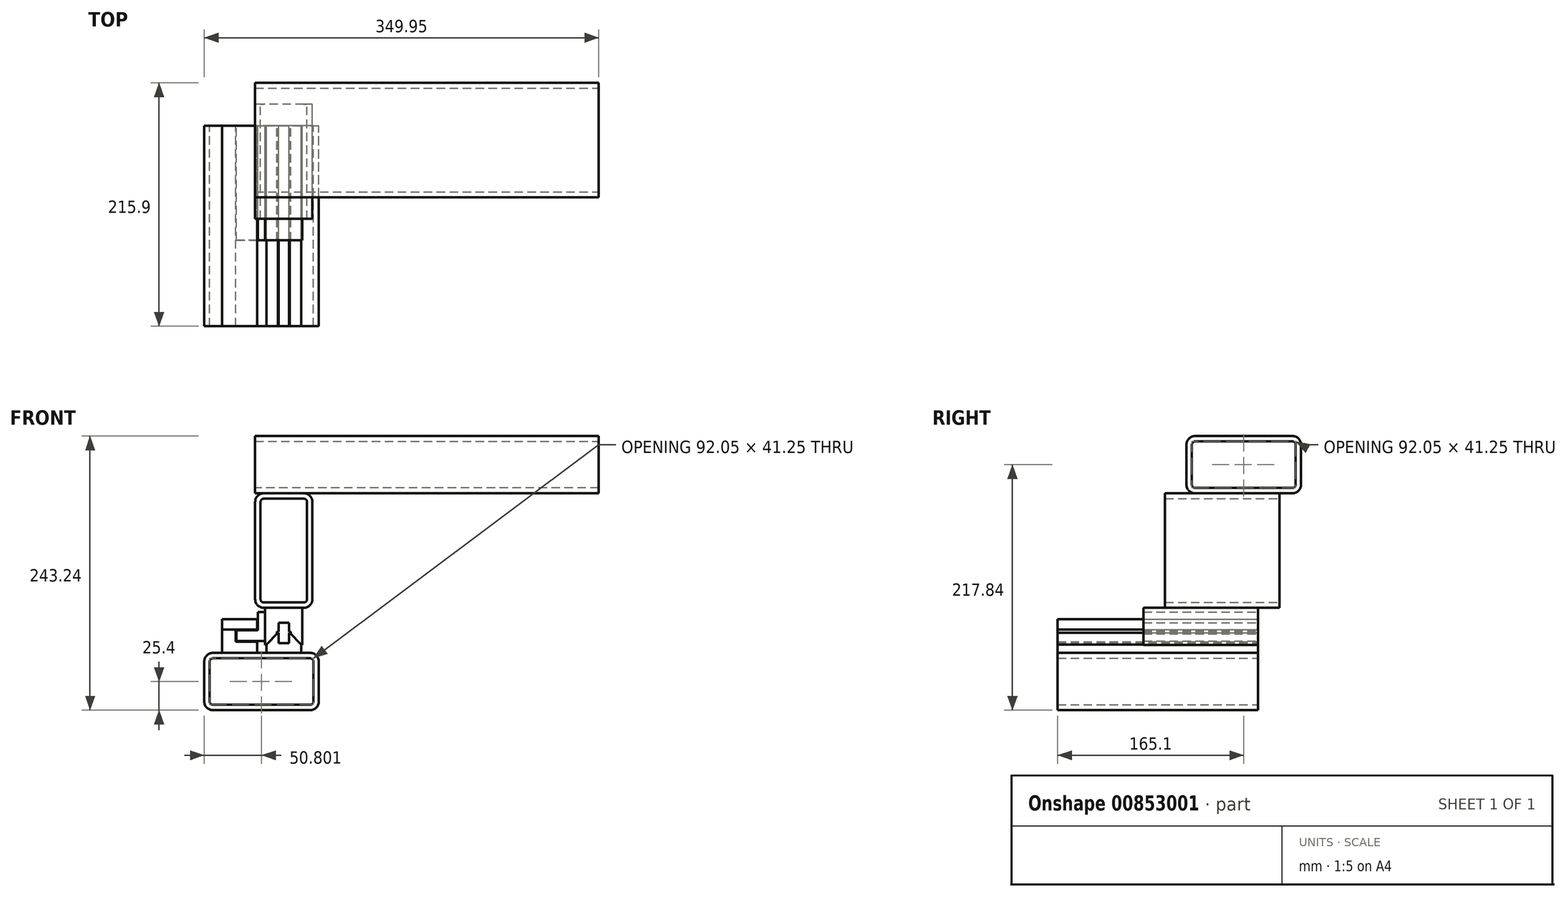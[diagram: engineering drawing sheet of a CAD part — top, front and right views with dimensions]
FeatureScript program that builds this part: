
annotation { "Feature Type Name" : "Feature", "Feature Type Description" : "" }
export const myFeature = defineFeature(function(context is Context, id is Id, definition is map)
    precondition{}
    {
        {
            var Q0;
            Q0=qCreatedBy(makeId("Front.planeOp"),FACE);
            var sketch = newSketch(context, id + "F0", { "sketchPlane" : qUnion([Q0])});
            skLineSegment(sketch, "E0", {"start": v(0, 0) * mm, "end": v(15.36, 0) * mm});
            skLineSegment(sketch, "E1", {"start": v(15.36, 0) * mm, "end": v(15.36, 7.56) * mm});
            skLineSegment(sketch, "E2", {"start": v(15.36, 7.56) * mm, "end": v(5.14, 17.78) * mm});
            skLineSegment(sketch, "E3", {"start": v(5.14, 17.78) * mm, "end": v(4.5, 17.78) * mm});
            skLineSegment(sketch, "E4", {"start": v(4.5, 17.78) * mm, "end": v(4.5, 8.78) * mm});
            skLineSegment(sketch, "E5", {"start": v(4.5, 8.78) * mm, "end": v(0, 8.78) * mm});
            skLineSegment(sketch, "E6", {"start": v(15.36, 7.56) * mm, "end": v(15.9, 7.02) * mm});
            skLineSegment(sketch, "E7", {"start": v(15.9, 7.02) * mm, "end": v(16.51, 7.02) * mm});
            skLineSegment(sketch, "E8", {"start": v(16.51, 7.02) * mm, "end": v(16.51, 40.04) * mm});
            skLineSegment(sketch, "E9", {"start": v(16.51, 40.04) * mm, "end": v(0, 40.04) * mm});
            skLineSegment(sketch, "E10", {"start": v(6.12, 16.8) * mm, "end": v(6.12, 18.78) * mm});
            skLineSegment(sketch, "E11", {"start": v(6.12, 18.78) * mm, "end": v(4.5, 18.78) * mm});
            skLineSegment(sketch, "E12", {"start": v(4.5, 18.78) * mm, "end": v(4.5, 26.78) * mm});
            skLineSegment(sketch, "E13", {"start": v(4.5, 26.78) * mm, "end": v(0, 26.78) * mm});
            skLineSegment(sketch, "E14.MirrorCS", {"start": v(-4.5, 8.78) * mm, "end": v(0, 8.78) * mm});
            skLineSegment(sketch, "E15.MirrorCS", {"start": v(0, 0) * mm, "end": v(-15.36, 0) * mm});
            skLineSegment(sketch, "E16.MirrorCS", {"start": v(-15.36, 0) * mm, "end": v(-15.36, 7.56) * mm});
            skLineSegment(sketch, "E17.MirrorCS", {"start": v(-4.5, 17.78) * mm, "end": v(-4.5, 8.78) * mm});
            skLineSegment(sketch, "E18.MirrorCS", {"start": v(-5.14, 17.78) * mm, "end": v(-4.5, 17.78) * mm});
            skLineSegment(sketch, "E19.MirrorCS", {"start": v(-15.36, 7.56) * mm, "end": v(-5.14, 17.78) * mm});
            skLineSegment(sketch, "E20.MirrorCS", {"start": v(-6.12, 16.8) * mm, "end": v(-6.12, 18.78) * mm});
            skLineSegment(sketch, "E21.MirrorCS", {"start": v(-6.12, 18.78) * mm, "end": v(-4.5, 18.78) * mm});
            skLineSegment(sketch, "E22.MirrorCS", {"start": v(-4.5, 18.78) * mm, "end": v(-4.5, 26.78) * mm});
            skLineSegment(sketch, "E23.MirrorCS", {"start": v(-15.9, 7.02) * mm, "end": v(-16.51, 7.02) * mm});
            skLineSegment(sketch, "E24.MirrorCS", {"start": v(-16.51, 7.02) * mm, "end": v(-16.51, 40.04) * mm});
            skLineSegment(sketch, "E25.MirrorCS", {"start": v(-4.5, 26.78) * mm, "end": v(0, 26.78) * mm});
            skLineSegment(sketch, "E26.MirrorCS", {"start": v(-16.51, 40.04) * mm, "end": v(0, 40.04) * mm});
            skLineSegment(sketch, "E27", {"start": v(5.14, 17.78) * mm, "end": v(0, 22.92) * mm, "construction": true});
            skLineSegment(sketch, "E28", {"start": v(-15.36, 7.56) * mm, "end": v(-15.9, 7.02) * mm});
            skSolve(sketch);
        }
        {
            var Q0;
            Q0=makeQuery(id+"F0.imprint","IMPRINT",FACE,{"disambiguationData":[TD([[makeQuery(id+"F0.imprint","IMPRINT",EDGE,{"derivedFrom":sQuery(id+"F0.wireOp",EDGE,"E0")}),1.0]])]});
            extrude(context, id + "F1", {"entities" : qUnion([Q0]), "depth" : 177.8 * mm, "offsetDistance" : 25.4 * mm});
        }
        {
            var Q0;
            {var subQ2=sQuery(id+"F0.wireOp",EDGE,"E7");Q0=makeQuery(id+"F0.imprint","IMPRINT",FACE,{"disambiguationData":[TD([[makeQuery(id+"F0.imprint","IMPRINT",EDGE,{"derivedFrom":subQ2}),1.0]])]});}
            extrude(context, id + "F2", {"entities" : qUnion([Q0]), "depth" : 101.6 * mm, "offsetDistance" : 25.4 * mm});
        }
        {
            var Q0;
            Q0=qCreatedBy(makeId("Front.planeOp"),FACE);
            var sketch = newSketch(context, id + "F3", { "sketchPlane" : qUnion([Q0])});
            skLineSegment(sketch, "E29.0", {"start": v(-15.36, 0) * mm, "end": v(-15.36, 7.56) * mm});
            skLineSegment(sketch, "E30", {"start": v(-15.36, 0) * mm, "end": v(-54.86, 0) * mm});
            skLineSegment(sketch, "E31", {"start": v(-54.86, 0) * mm, "end": v(-54.86, 29.93) * mm});
            skLineSegment(sketch, "E32", {"start": v(-54.86, 29.93) * mm, "end": v(-23.64, 29.93) * mm});
            skLineSegment(sketch, "E33", {"start": v(-23.64, 29.93) * mm, "end": v(-23.64, 20.74) * mm});
            skLineSegment(sketch, "E34", {"start": v(-23.64, 20.74) * mm, "end": v(-42.7, 20.74) * mm});
            skLineSegment(sketch, "E35", {"start": v(-42.7, 20.74) * mm, "end": v(-54.86, 20.74) * mm});
            skLineSegment(sketch, "E36.0", {"start": v(-16.51, 7.02) * mm, "end": v(-16.51, 40.04) * mm});
            skLineSegment(sketch, "E37", {"start": v(-41.93, 19.98) * mm, "end": v(-41.93, 10.63) * mm});
            skLineSegment(sketch, "E38", {"start": v(-41.93, 10.63) * mm, "end": v(-16.51, 10.63) * mm});
            skLineSegment(sketch, "E39", {"start": v(-22.86, 19.98) * mm, "end": v(-22.86, 36.45) * mm});
            skLineSegment(sketch, "E40", {"start": v(-22.86, 36.45) * mm, "end": v(-16.51, 36.29) * mm});
            skLineSegment(sketch, "E41", {"start": v(-22.86, 19.98) * mm, "end": v(-41.93, 19.98) * mm});
            skLineSegment(sketch, "E42", {"start": v(-23.64, 7.56) * mm, "end": v(-23.64, 9.87) * mm});
            skLineSegment(sketch, "E43", {"start": v(-23.64, 9.87) * mm, "end": v(-42.7, 9.87) * mm});
            skLineSegment(sketch, "E44", {"start": v(-42.7, 9.87) * mm, "end": v(-42.7, 20.74) * mm});
            skLineSegment(sketch, "E45", {"start": v(-42.7, 15.75) * mm, "end": v(-41.93, 15.75) * mm, "construction": true});
            skLineSegment(sketch, "E46", {"start": v(-33.1, 20.74) * mm, "end": v(-33.1, 19.98) * mm, "construction": true});
            skLineSegment(sketch, "E47", {"start": v(-28.61, 9.87) * mm, "end": v(-28.61, 10.63) * mm, "construction": true});
            skLineSegment(sketch, "E48", {"start": v(-23.64, 7.56) * mm, "end": v(-23.64, 4.69) * mm});
            skLineSegment(sketch, "E49", {"start": v(-23.64, 4.69) * mm, "end": v(-23.64, 0) * mm});
            skLineSegment(sketch, "E50", {"start": v(-54.86, 0) * mm, "end": v(-54.86, -7.97) * mm});
            skLineSegment(sketch, "E51", {"start": v(-54.86, -7.97) * mm, "end": v(20.19, -7.97) * mm});
            skLineSegment(sketch, "E52", {"start": v(20.19, -7.97) * mm, "end": v(20.19, 0) * mm});
            skLineSegment(sketch, "E53", {"start": v(20.19, 0) * mm, "end": v(-15.36, 0) * mm});
            skSolve(sketch);
        }
        {
            var Q0;
            Q0=makeQuery(id+"F3.imprint","IMPRINT",FACE,{"disambiguationData":[TD([[makeQuery(id+"F3.imprint","IMPRINT",EDGE,{"derivedFrom":sQuery(id+"F3.wireOp",EDGE,"E37")}),1.0]])]});
            var Q1;
            Q1=makeQuery(id+"F2.opExtrude","CAP_FACE",FACE,{"disambiguationData":[OSD([sQuery(id+"F0.wireOp",EDGE,"E2"),sQuery(id+"F0.wireOp",EDGE,"E7"),sQuery(id+"F0.wireOp",EDGE,"E8"),sQuery(id+"F0.wireOp",EDGE,"E9"),sQuery(id+"F0.wireOp",EDGE,"E10"),sQuery(id+"F0.wireOp",EDGE,"E11"),sQuery(id+"F0.wireOp",EDGE,"E12"),sQuery(id+"F0.wireOp",EDGE,"E13"),sQuery(id+"F0.wireOp",EDGE,"E19.MirrorCS"),sQuery(id+"F0.wireOp",EDGE,"E20.MirrorCS"),sQuery(id+"F0.wireOp",EDGE,"E21.MirrorCS"),sQuery(id+"F0.wireOp",EDGE,"E22.MirrorCS"),sQuery(id+"F0.wireOp",EDGE,"E23.MirrorCS"),sQuery(id+"F0.wireOp",EDGE,"E24.MirrorCS"),sQuery(id+"F0.wireOp",EDGE,"E25.MirrorCS"),sQuery(id+"F0.wireOp",EDGE,"E26.MirrorCS")])],"isStart":false});
            extrude(context, id + "F4", {"entities" : qUnion([Q0]), "endBound" : BoundingType.UP_TO_SURFACE, "depth" : 25.4 * mm, "endBoundEntityFace" : qUnion([Q1]), "offsetDistance" : 25.4 * mm});
        }
        {
            var Q0;
            {var subQ0=sQuery(id+"F3.wireOp",EDGE,"E32");Q0=makeQuery(id+"F3.imprint","IMPRINT",FACE,{"disambiguationData":[TD([[makeQuery(id+"F3.imprint","IMPRINT",EDGE,{"derivedFrom":subQ0}),-1.0]])]});}
            var Q1;
            Q1=makeQuery(id+"F1.opExtrude","CAP_FACE",FACE,{"disambiguationData":[OSD([sQuery(id+"F0.wireOp",EDGE,"E0"),sQuery(id+"F0.wireOp",EDGE,"E1"),sQuery(id+"F0.wireOp",EDGE,"E2"),sQuery(id+"F0.wireOp",EDGE,"E3"),sQuery(id+"F0.wireOp",EDGE,"E4"),sQuery(id+"F0.wireOp",EDGE,"E5"),sQuery(id+"F0.wireOp",EDGE,"E6"),sQuery(id+"F0.wireOp",EDGE,"E14.MirrorCS"),sQuery(id+"F0.wireOp",EDGE,"E15.MirrorCS"),sQuery(id+"F0.wireOp",EDGE,"E16.MirrorCS"),sQuery(id+"F0.wireOp",EDGE,"E17.MirrorCS"),sQuery(id+"F0.wireOp",EDGE,"E18.MirrorCS"),sQuery(id+"F0.wireOp",EDGE,"E19.MirrorCS")])],"isStart":false});
            extrude(context, id + "F5", {"entities" : qUnion([Q0]), "endBound" : BoundingType.UP_TO_SURFACE, "depth" : 25.4 * mm, "endBoundEntityFace" : qUnion([Q1]), "offsetDistance" : 25.4 * mm});
        }
        {
            var Q0;
            {var subQ0=sQuery(id+"F3.wireOp",EDGE,"E35");Q0=makeQuery(id+"F3.imprint","IMPRINT",FACE,{"disambiguationData":[TD([[makeQuery(id+"F3.imprint","IMPRINT",EDGE,{"derivedFrom":subQ0}),1.0]])]});}
            var Q1;
            Q1=makeQuery(id+"F5.opExtrude","CAP_FACE",FACE,{"disambiguationData":[OSD([sQuery(id+"F3.wireOp",EDGE,"E29.0"),sQuery(id+"F3.wireOp",EDGE,"E30"),sQuery(id+"F3.wireOp",EDGE,"E31"),sQuery(id+"F3.wireOp",EDGE,"E35"),sQuery(id+"F3.wireOp",EDGE,"DQE3j6KB-5Aju-39En-5gZ4-T2iJxYTfEG1l"),sQuery(id+"F3.wireOp",EDGE,"E42"),sQuery(id+"F3.wireOp",EDGE,"E43"),sQuery(id+"F3.wireOp",EDGE,"E44")])],"isStart":false});
            extrude(context, id + "F6", {"entities" : qUnion([Q0]), "endBound" : BoundingType.UP_TO_SURFACE, "depth" : 25.4 * mm, "endBoundEntityFace" : qUnion([Q1]), "offsetDistance" : 25.4 * mm});
        }
        {
            var Q0;
            Q0=qCreatedBy(makeId("Front.planeOp"),FACE);
            var sketch = newSketch(context, id + "F7", { "sketchPlane" : qUnion([Q0])});
            skPoint(sketch, "E54.0", {"position": v(15.36, 0) * mm});
            skPoint(sketch, "E55.0", {"position": v(-54.86, 0) * mm});
            skLineSegment(sketch, "E56", {"start": v(-54.86, 0) * mm, "end": v(15.36, 0) * mm, "construction": true});
            skLineSegment(sketch, "E57", {"start": v(-19.75, 0) * mm, "end": v(-19.75, -25.4) * mm, "construction": true});
            skLineSegment(sketch, "E58.bottom", {"start": v(31.05, 0) * mm, "end": v(-70.55, 0) * mm});
            skLineSegment(sketch, "E58.top", {"start": v(31.05, -50.8) * mm, "end": v(-70.55, -50.8) * mm});
            skLineSegment(sketch, "E58.left", {"start": v(31.05, 0) * mm, "end": v(31.05, -50.8) * mm});
            skLineSegment(sketch, "E58.right", {"start": v(-70.55, 0) * mm, "end": v(-70.55, -50.8) * mm});
            skPoint(sketch, "E58.middle", {"position": v(-19.75, -25.4) * mm});
            skSolve(sketch);
        }
        {
            var Q0;
            Q0 = qSketchRegion(id + "F7", true);
            var Q1;
            Q1=makeQuery(id+"F6.opExtrude","CAP_FACE",FACE,{"disambiguationData":[OSD([sQuery(id+"F3.wireOp",EDGE,"E30"),sQuery(id+"F3.wireOp",EDGE,"E31"),sQuery(id+"F3.wireOp",EDGE,"E35"),sQuery(id+"F3.wireOp",EDGE,"E42"),sQuery(id+"F3.wireOp",EDGE,"E43"),sQuery(id+"F3.wireOp",EDGE,"E44"),sQuery(id+"F3.wireOp",EDGE,"E48"),sQuery(id+"F3.wireOp",EDGE,"E49")])],"isStart":false});
            extrude(context, id + "F8", {"entities" : qUnion([Q0]), "endBound" : BoundingType.UP_TO_SURFACE, "depth" : 25.4 * mm, "endBoundEntityFace" : qUnion([Q1]), "offsetDistance" : 25.4 * mm});
        }
        {
            var Q0;
            Q0=makeQuery(id+"F8.opExtrude","SWEPT_EDGE",EDGE,{"disambiguationData":[OSD([sQuery(id+"F7.wireOp",EDGE,"E58.bottom"),sQuery(id+"F7.wireOp",EDGE,"E58.right")])]});
            var Q1;
            Q1=makeQuery(id+"F8.opExtrude","SWEPT_EDGE",EDGE,{"disambiguationData":[OSD([sQuery(id+"F7.wireOp",EDGE,"E58.bottom"),sQuery(id+"F7.wireOp",EDGE,"E58.left")])]});
            var Q2;
            Q2=makeQuery(id+"F8.opExtrude","SWEPT_EDGE",EDGE,{"disambiguationData":[OSD([sQuery(id+"F7.wireOp",EDGE,"E58.top"),sQuery(id+"F7.wireOp",EDGE,"E58.right")])]});
            var Q3;
            Q3=makeQuery(id+"F8.opExtrude","SWEPT_EDGE",EDGE,{"disambiguationData":[OSD([sQuery(id+"F7.wireOp",EDGE,"E58.top"),sQuery(id+"F7.wireOp",EDGE,"E58.left")])]});
            fillet(context, id + "F9", {"entities" : qUnion([Q0, Q1, Q2, Q3]), "radius" : 7.62 * mm, "tangentPropagation" : true, "allowEdgeOverflow" : false});
        }
        {
            var Q0;
            Q0=makeQuery(id+"F8.opExtrude","CAP_FACE",FACE,{"disambiguationData":[OSD([sQuery(id+"F7.wireOp",EDGE,"E58.bottom"),sQuery(id+"F7.wireOp",EDGE,"E58.top"),sQuery(id+"F7.wireOp",EDGE,"E58.left"),sQuery(id+"F7.wireOp",EDGE,"E58.right")])],"isStart":false});
            shell(context, id + "F10", {"entities" : qUnion([Q0]), "thickness" : 4.78 * mm});
        }
        {
            var Q0;
            Q0=makeQuery(id+"F10.opShell","OFFSET_FACE",FACE,{"disambiguationData":[OSD([sQuery(id+"F7.wireOp",EDGE,"E58.bottom"),sQuery(id+"F7.wireOp",EDGE,"E58.top"),sQuery(id+"F7.wireOp",EDGE,"E58.left"),sQuery(id+"F7.wireOp",EDGE,"E58.right")])]});
            extrude(context, id + "F11", {"entities" : qUnion([Q0]), "operationType" : NewBodyOperationType.REMOVE, "oppositeDirection" : true, "depth" : 25.4 * mm, "offsetDistance" : 25.4 * mm});
        }
        {
            var Q0;
            Q0=qCreatedBy(makeId("Front.planeOp"),FACE);
            var sketch = newSketch(context, id + "F12", { "sketchPlane" : qUnion([Q0])});
            skPoint(sketch, "E59.0", {"position": v(0, 40.04) * mm});
            skLineSegment(sketch, "E60.bottom", {"start": v(25.4, 40.04) * mm, "end": v(-25.4, 40.04) * mm});
            skLineSegment(sketch, "E60.top", {"start": v(25.4, 141.64) * mm, "end": v(-25.4, 141.64) * mm});
            skLineSegment(sketch, "E60.left", {"start": v(25.4, 40.04) * mm, "end": v(25.4, 141.64) * mm});
            skLineSegment(sketch, "E60.right", {"start": v(-25.4, 40.04) * mm, "end": v(-25.4, 141.64) * mm});
            skPoint(sketch, "E60.middle", {"position": v(0, 90.84) * mm});
            skSolve(sketch);
        }
        {
            var Q0;
            Q0 = qSketchRegion(id + "F12", true);
            extrude(context, id + "F13", {"entities" : qUnion([Q0]), "depth" : 82.55 * mm, "offsetDistance" : 25.4 * mm, "hasSecondDirection" : true, "secondDirectionOppositeDirection" : true, "secondDirectionDepth" : 19.05 * mm});
        }
        {
            var Q0;
            Q0=makeQuery(id+"F13.opExtrude","SWEPT_EDGE",EDGE,{"disambiguationData":[OSD([sQuery(id+"F12.wireOp",EDGE,"E60.top"),sQuery(id+"F12.wireOp",EDGE,"E60.left")])]});
            var Q1;
            Q1=makeQuery(id+"F13.opExtrude","SWEPT_EDGE",EDGE,{"disambiguationData":[OSD([sQuery(id+"F12.wireOp",EDGE,"E60.bottom"),sQuery(id+"F12.wireOp",EDGE,"E60.left")])]});
            var Q2;
            Q2=makeQuery(id+"F13.opExtrude","SWEPT_EDGE",EDGE,{"disambiguationData":[OSD([sQuery(id+"F12.wireOp",EDGE,"E60.bottom"),sQuery(id+"F12.wireOp",EDGE,"E60.right")])]});
            var Q3;
            Q3=makeQuery(id+"F13.opExtrude","SWEPT_EDGE",EDGE,{"disambiguationData":[OSD([sQuery(id+"F12.wireOp",EDGE,"E60.top"),sQuery(id+"F12.wireOp",EDGE,"E60.right")])]});
            fillet(context, id + "F14", {"entities" : qUnion([Q0, Q1, Q2, Q3]), "radius" : 7.62 * mm, "tangentPropagation" : true, "allowEdgeOverflow" : false});
        }
        {
            var Q0;
            Q0=makeQuery(id+"F13.opExtrude","CAP_FACE",FACE,{"disambiguationData":[OSD([sQuery(id+"F12.wireOp",EDGE,"E60.bottom"),sQuery(id+"F12.wireOp",EDGE,"E60.top"),sQuery(id+"F12.wireOp",EDGE,"E60.left"),sQuery(id+"F12.wireOp",EDGE,"E60.right")])],"isStart":false});
            shell(context, id + "F15", {"entities" : qUnion([Q0]), "thickness" : 4.78 * mm});
        }
        {
            var Q0;
            Q0=makeQuery(id+"F15.opShell","OFFSET_FACE",FACE,{"disambiguationData":[OSD([sQuery(id+"F12.wireOp",EDGE,"E60.bottom"),sQuery(id+"F12.wireOp",EDGE,"E60.top"),sQuery(id+"F12.wireOp",EDGE,"E60.left"),sQuery(id+"F12.wireOp",EDGE,"E60.right")])]});
            extrude(context, id + "F16", {"entities" : qUnion([Q0]), "operationType" : NewBodyOperationType.REMOVE, "oppositeDirection" : true, "depth" : 25.4 * mm, "offsetDistance" : 25.4 * mm});
        }
        {
            var Q0;
            Q0=makeQuery(id+"F13.opExtrude","SWEPT_FACE",FACE,{"disambiguationData":[OSD([sQuery(id+"F12.wireOp",EDGE,"E60.right")])]});
            var sketch = newSketch(context, id + "F17", { "sketchPlane" : qUnion([Q0])});
            skLineSegment(sketch, "E61.0", {"start": v(-19.05, 141.64) * mm, "end": v(82.55, 141.64) * mm});
            skLineSegment(sketch, "E62.bottom", {"start": v(63.5, 141.64) * mm, "end": v(-38.1, 141.64) * mm});
            skLineSegment(sketch, "E62.top", {"start": v(63.5, 192.44) * mm, "end": v(-38.1, 192.44) * mm});
            skLineSegment(sketch, "E62.left", {"start": v(63.5, 141.64) * mm, "end": v(63.5, 192.44) * mm});
            skLineSegment(sketch, "E62.right", {"start": v(-38.1, 141.64) * mm, "end": v(-38.1, 192.44) * mm});
            skPoint(sketch, "E62.middle", {"position": v(12.7, 167.04) * mm});
            skPoint(sketch, "E62.middle.positionSnap0", {"position": v(31.75, 141.64) * mm});
            skPoint(sketch, "E62.centerSnap0", {"position": v(31.75, 141.64) * mm});
            skPoint(sketch, "E63", {"position": v(12.7, 141.64) * mm});
            skSolve(sketch);
        }
        {
            var Q0;
            Q0 = qSketchRegion(id + "F17", true);
            extrude(context, id + "F18", {"entities" : qUnion([Q0]), "oppositeDirection" : true, "depth" : 304.8 * mm, "offsetDistance" : 25.4 * mm});
        }
        {
            var Q0;
            Q0=makeQuery(id+"F18.opExtrude","SWEPT_EDGE",EDGE,{"disambiguationData":[OSD([sQuery(id+"F17.wireOp",EDGE,"E62.bottom"),sQuery(id+"F17.wireOp",EDGE,"E62.right")])]});
            var Q1;
            Q1=makeQuery(id+"F18.opExtrude","SWEPT_EDGE",EDGE,{"disambiguationData":[OSD([sQuery(id+"F17.wireOp",EDGE,"E62.bottom"),sQuery(id+"F17.wireOp",EDGE,"E62.left")])]});
            var Q2;
            Q2=makeQuery(id+"F18.opExtrude","SWEPT_EDGE",EDGE,{"disambiguationData":[OSD([sQuery(id+"F17.wireOp",EDGE,"E62.top"),sQuery(id+"F17.wireOp",EDGE,"E62.left")])]});
            var Q3;
            Q3=makeQuery(id+"F18.opExtrude","SWEPT_EDGE",EDGE,{"disambiguationData":[OSD([sQuery(id+"F17.wireOp",EDGE,"E62.top"),sQuery(id+"F17.wireOp",EDGE,"E62.right")])]});
            fillet(context, id + "F19", {"entities" : qUnion([Q0, Q1, Q2, Q3]), "radius" : 7.62 * mm, "tangentPropagation" : true, "allowEdgeOverflow" : false});
        }
        {
            var Q0;
            Q0=makeQuery(id+"F18.opExtrude","CAP_FACE",FACE,{"disambiguationData":[OSD([sQuery(id+"F17.wireOp",EDGE,"E62.bottom"),sQuery(id+"F17.wireOp",EDGE,"E62.top"),sQuery(id+"F17.wireOp",EDGE,"E62.left"),sQuery(id+"F17.wireOp",EDGE,"E62.right")])],"isStart":true});
            shell(context, id + "F20", {"entities" : qUnion([Q0]), "thickness" : 4.78 * mm});
        }
        {
            var Q0;
            Q0=makeQuery(id+"F20.opShell","OFFSET_FACE",FACE,{"disambiguationData":[OSD([sQuery(id+"F17.wireOp",EDGE,"E62.bottom"),sQuery(id+"F17.wireOp",EDGE,"E62.top"),sQuery(id+"F17.wireOp",EDGE,"E62.left"),sQuery(id+"F17.wireOp",EDGE,"E62.right")])]});
            extrude(context, id + "F21", {"entities" : qUnion([Q0]), "operationType" : NewBodyOperationType.REMOVE, "oppositeDirection" : true, "depth" : 25.4 * mm, "offsetDistance" : 25.4 * mm});
        }
    });
